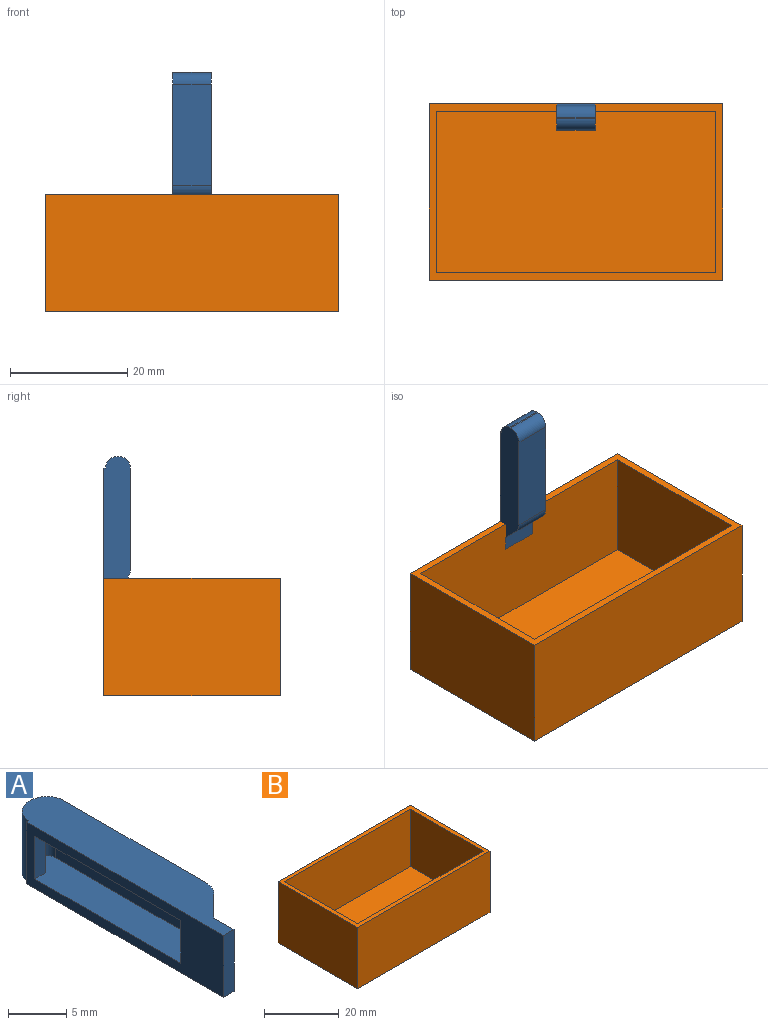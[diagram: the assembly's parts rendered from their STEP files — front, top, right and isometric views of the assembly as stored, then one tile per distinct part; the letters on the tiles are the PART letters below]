
ASSEMBLY  parts=2 mates=1
PART A: 24 faces, bbox 4.5x25.9x6.5 mm
  f0: plane 6.5x2.5mm, normal (0.71,-0.71,0), area 23mm2, adj f11,f18,f19,f23
  f1: plane 4.5x1.27mm, normal (0,-1,0), area 5.7mm2, adj f2,f17,f20,f21
  f2: plane 4.5x1mm, normal (1,0,0), area 4.5mm2, adj f1,f5,f20,f21
  f3: cylinder r=0.5mm len=4.5mm, axis (0,0,-1), area 7.1mm2, adj f4,f10,f20,f21
  f4: plane 4.5x0.5mm, normal (0,1,0), area 2.2mm2, adj f3,f17,f20,f21
  f5: cylinder r=1mm len=4.5mm, axis (0,0,-1), area 7.1mm2, adj f2,f6,f20,f21
  f6: plane 4.5x0.23mm, normal (0,-1,0), area 1mm2, adj f5,f7,f20,f21
  f7: cylinder r=1mm len=4.5mm, axis (0,0,-1), area 7.1mm2, adj f6,f8,f20,f21
  f8: plane 17.23x4.5mm, normal (-1,0,0), area 77.5mm2, adj f7,f9,f20,f21
  f9: cylinder r=1.5mm len=4.5mm, axis (0,0,-1), area 10.6mm2, adj f8,f10,f20,f21
  f10: plane 4.5x0.5mm, normal (0,1,0), area 2.2mm2, adj f3,f9,f20,f21
  f11: cylinder r=2.5mm len=6.5mm, axis (0,0,-1), area 12.8mm2, adj f0,f12,f18,f19
  f12: plane 17.23x6.5mm, normal (1,0,0), area 112mm2, adj f11,f13,f18,f19
  f13: cylinder r=2mm len=6.5mm, axis (0,0,-1), area 20.4mm2, adj f12,f14,f18,f19
  f14: plane 6.5x0.23mm, normal (0,1,0), area 1.5mm2, adj f13,f15,f18,f19
  f15: cylinder r=2mm len=6.5mm, axis (0,0,-1), area 20.4mm2, adj f14,f16,f18,f19
  f16: plane 6.5x0.27mm, normal (0,1,0), area 1.8mm2, adj f15,f17,f18,f19
  f17: plane 23.92x6.5mm, normal (-1,0,0), area 75.7mm2, adj f1,f4,f16,f18,f19,f20,f21,f22
  f18: plane 25.92x4.5mm, normal (0,0,1), area 101.2mm2, adj f0,f11,f12,f13,f14,f15,f16,f17
  f19: plane 25.92x4.5mm, normal (0,0,-1), area 101.2mm2, adj f0,f11,f12,f13,f14,f15,f16,f17
  f20: plane 19.73x3.5mm, normal (0,0,-1), area 65.2mm2, adj f1,f2,f3,f4,f5,f6,f7,f8
  f21: plane 19.73x3.5mm, normal (0,0,1), area 65.2mm2, adj f1,f2,f3,f4,f5,f6,f7,f8
  f22: plane 6.5x1.27mm, normal (0,-1,0), area 8.3mm2, adj f17,f18,f19,f23
  f23: plane 6.5x2.43mm, normal (1,0,0), area 15.8mm2, adj f0,f18,f19,f22
PART B: 11 faces, bbox 50x30x20 mm
  f0: plane 50x30mm, normal (0,0,1), area 196.7mm2, adj f1,f2,f3,f4,f6,f7,f8,f9
  f1: plane 30x20mm, normal (-1,0,0), area 600mm2, adj f0,f2,f4,f5
  f2: plane 50x20mm, normal (0,-1,0), area 1000mm2, adj f0,f1,f3,f5
  f3: plane 30x20mm, normal (1,0,0), area 600mm2, adj f0,f2,f4,f5
  f4: plane 50x20mm, normal (0,1,0), area 1000mm2, adj f0,f1,f3,f5
  f5: plane 50x30mm, normal (0,0,-1), area 1500mm2, adj f1,f2,f3,f4
  f6: plane 27.46x18.73mm, normal (1,0,0), area 514.3mm2, adj f0,f7,f9,f10
  f7: plane 47.46x18.73mm, normal (0,1,0), area 888.9mm2, adj f0,f6,f8,f10
  f8: plane 27.46x18.73mm, normal (-1,0,0), area 514.3mm2, adj f0,f7,f9,f10
  f9: plane 47.46x18.73mm, normal (0,-1,0), area 888.9mm2, adj f0,f6,f8,f10
  f10: plane 47.46x27.46mm, normal (0,0,1), area 1303.3mm2, adj f6,f7,f8,f9
PLACE A rot(axis=(0.58,-0.58,-0.58),120deg) t=(25,30,35.91)mm
PLACE B t=(0,0,15.41)mm
MATE planar B.f4 <-> A.f17  axis (0,1,0) through (25,30,35.41)mm
